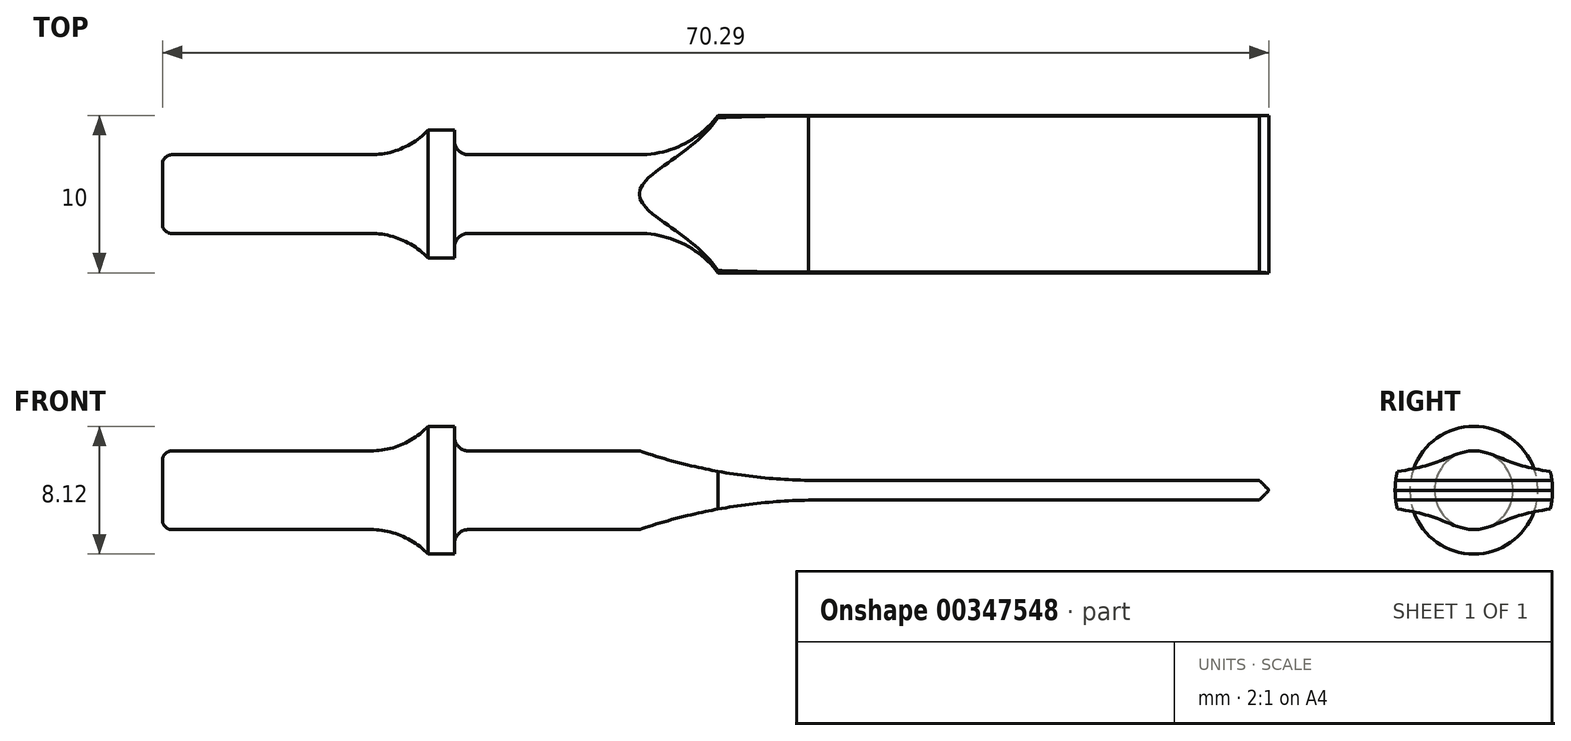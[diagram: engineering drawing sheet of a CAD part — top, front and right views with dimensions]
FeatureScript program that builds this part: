
annotation { "Feature Type Name" : "Feature", "Feature Type Description" : "" }
export const myFeature = defineFeature(function(context is Context, id is Id, definition is map)
    precondition{}
    {
        {
            var Q0;
            Q0=qCreatedBy(makeId("Front.planeOp"),FACE);
            var sketch = newSketch(context, id + "F0", { "sketchPlane" : qUnion([Q0])});
            skLineSegment(sketch, "E0", {"start": v(0, 0) * mm, "end": v(70.29, 0) * mm});
            skLineSegment(sketch, "E1", {"start": v(0, 0) * mm, "end": v(0, 1.9) * mm});
            skLineSegment(sketch, "E2", {"start": v(0.6, 2.5) * mm, "end": v(13.24, 2.5) * mm});
            skLineSegment(sketch, "E3", {"start": v(16.87, 4.06) * mm, "end": v(18.54, 4.06) * mm});
            skLineSegment(sketch, "E4", {"start": v(18.54, 4.06) * mm, "end": v(18.54, 3.4) * mm});
            skLineSegment(sketch, "E5", {"start": v(70.29, 0) * mm, "end": v(70.29, 5) * mm});
            skLineSegment(sketch, "E6.0", {"start": v(30.29, 0) * mm, "end": v(30.29, 2.5) * mm, "construction": true});
            skLineSegment(sketch, "E7.0", {"start": v(35.29, 0) * mm, "end": v(35.29, 5) * mm, "construction": true});
            skLineSegment(sketch, "E8", {"start": v(70.29, 5) * mm, "end": v(35.29, 5) * mm});
            skLineSegment(sketch, "E9.trimOffspring", {"start": v(19.44, 2.5) * mm, "end": v(30.29, 2.5) * mm});
            skArc(sketch, "E10", {"start": v(30.29, 2.5) * mm, "mid": v(33.08, 3.16) * mm, "end": v(35.29, 5) * mm});
            skArc(sketch, "E11", {"start": v(13.24, 2.5) * mm, "mid": v(15.22, 2.9) * mm, "end": v(16.87, 4.06) * mm});
            skPoint(sketch, "E12.visualSharp", {"position": v(0, 2.5) * mm});
            skArc(sketch, "E12.filletArc", {"start": v(0.6, 2.5) * mm, "mid": v(0.18, 2.32) * mm, "end": v(0, 1.9) * mm});
            skPoint(sketch, "E13.newPointA", {"position": v(18.54, 0) * mm});
            skArc(sketch, "E13.filletArc", {"start": v(18.54, 3.4) * mm, "mid": v(18.8, 2.76) * mm, "end": v(19.44, 2.5) * mm});
            skSolve(sketch);
        }
        {
            var Q0;
            Q0=makeQuery(id+"F0.imprint","IMPRINT",FACE,{"disambiguationData":[TD([[makeQuery(id+"F0.imprint","IMPRINT",EDGE,{"derivedFrom":sQuery(id+"F0.wireOp",EDGE,"E0")}),1.0]])]});
            var Q1;
            Q1=sQuery(id+"F0.wireOp",EDGE,"E0");
            revolve(context, id + "F1", {"entities" : qUnion([Q0]), "axis" : qUnion([Q1]), "revolveType" : RevolveType.FULL});
        }
        {
            var Q0;
            Q0=qCreatedBy(makeId("Front.planeOp"),FACE);
            var sketch = newSketch(context, id + "F2", { "sketchPlane" : qUnion([Q0])});
            skLineSegment(sketch, "E14", {"start": v(0, 0) * mm, "end": v(70.29, 0) * mm, "construction": true});
            skLineSegment(sketch, "E15", {"start": v(70.29, 0) * mm, "end": v(70.29, 10.12) * mm, "construction": true});
            skLineSegment(sketch, "E16.0", {"start": v(30.29, 0) * mm, "end": v(30.29, 10.12) * mm, "construction": true});
            skLineSegment(sketch, "E17.0", {"start": v(0, 2.5) * mm, "end": v(70.29, 2.5) * mm, "construction": true});
            skPoint(sketch, "E18", {"position": v(30.29, 2.5) * mm});
            skLineSegment(sketch, "E19.0", {"start": v(41.02, 0.63) * mm, "end": v(69.66, 0.63) * mm});
            skArc(sketch, "E20", {"start": v(30.29, 2.5) * mm, "mid": v(35.87, 1.1) * mm, "end": v(41.61, 0.63) * mm});
            skLineSegment(sketch, "E21", {"start": v(70.29, 0) * mm, "end": v(70.29, 0.63) * mm});
            skLineSegment(sketch, "E22", {"start": v(70.29, 0) * mm, "end": v(69.66, 0.63) * mm});
            skLineSegment(sketch, "E23", {"start": v(30.29, 2.5) * mm, "end": v(30.29, 14.09) * mm});
            skLineSegment(sketch, "E24", {"start": v(30.29, 14.09) * mm, "end": v(73.75, 14.09) * mm});
            skLineSegment(sketch, "E25", {"start": v(73.75, 14.09) * mm, "end": v(70.29, 0) * mm});
            skLineSegment(sketch, "E26.MirrorCS", {"start": v(30.29, -2.5) * mm, "end": v(30.29, -14.09) * mm});
            skArc(sketch, "E27.MirrorCS", {"start": v(30.29, -2.5) * mm, "mid": v(35.87, -1.1) * mm, "end": v(41.61, -0.63) * mm});
            skLineSegment(sketch, "E28.MirrorCS", {"start": v(41.02, -0.63) * mm, "end": v(69.66, -0.63) * mm});
            skLineSegment(sketch, "E29.MirrorCS", {"start": v(70.29, 0) * mm, "end": v(69.66, -0.63) * mm});
            skLineSegment(sketch, "E30.MirrorCS", {"start": v(73.75, -14.09) * mm, "end": v(70.29, 0) * mm});
            skLineSegment(sketch, "E31.MirrorCS", {"start": v(30.29, -14.09) * mm, "end": v(73.75, -14.09) * mm});
            skSolve(sketch);
        }
        {
            var Q0;
            {var subQ2=sQuery(id+"F2.wireOp",EDGE,"E19.0");Q0=makeQuery(id+"F2.imprint","IMPRINT",FACE,{"disambiguationData":[TD([[makeQuery(id+"F2.imprint","IMPRINT",EDGE,{"derivedFrom":subQ2}),1.0]])]});}
            var Q1;
            {var subQ2=sQuery(id+"F2.wireOp",EDGE,"E26.MirrorCS");Q1=makeQuery(id+"F2.imprint","IMPRINT",FACE,{"disambiguationData":[TD([[makeQuery(id+"F2.imprint","IMPRINT",EDGE,{"derivedFrom":subQ2}),1.0]])]});}
            extrude(context, id + "F3", {"entities" : qUnion([Q0, Q1]), "operationType" : NewBodyOperationType.REMOVE, "oppositeDirection" : true, "depth" : 25 * mm});
        }
        {
            var Q0;
            Q0 = qSketchRegion(id + "F2", true);
            extrude(context, id + "F4", {"entities" : qUnion([Q0]), "operationType" : NewBodyOperationType.REMOVE, "depth" : 25 * mm});
        }
    });
